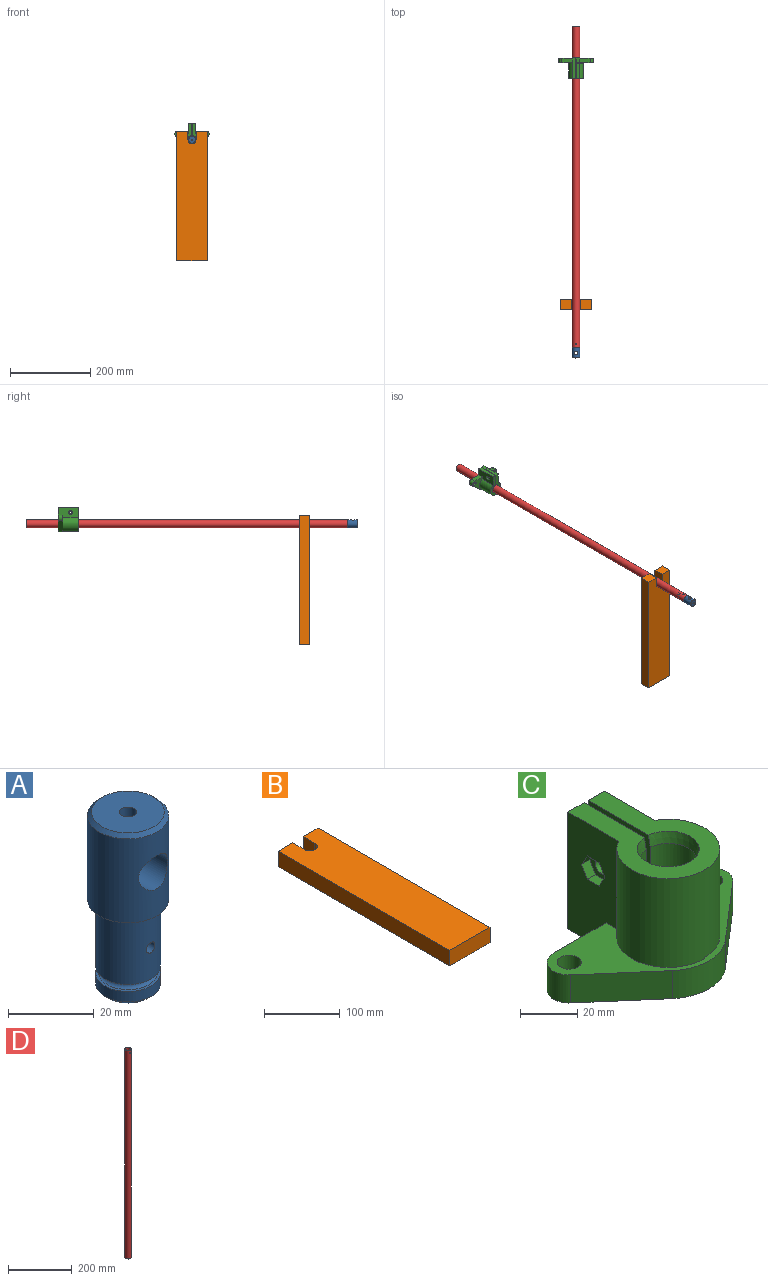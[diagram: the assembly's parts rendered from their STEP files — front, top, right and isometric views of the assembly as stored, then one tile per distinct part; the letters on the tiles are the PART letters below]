
ASSEMBLY  parts=4 mates=3
PART A: 16 faces, bbox 19x19x50 mm
  f0: cylinder r=2mm len=8.19mm, axis (0,0,-1), area 100.1mm2, adj f6,f13
  f1: cylinder r=7.6mm len=15.2mm, axis (0,0,-1), area 143.3mm2, adj f10,f12
  f2: cylinder r=2mm len=33.19mm, axis (0,0,-1), area 399.9mm2, adj f4,f13,f14,f15
  f3: cylinder r=7.6mm len=19.01mm, axis (0,0,-1), area 894.3mm2, adj f7,f9,f14,f15
  f4: plane 13.2x13.2mm, normal (0,0,-1), area 124.3mm2, adj f2,f12
  f5: cylinder r=9.5mm len=24mm, axis (0,0,-1), area 1285.8mm2, adj f7,f11,f13
  f6: plane 17x17mm, normal (0,0,1), area 214.4mm2, adj f0,f11
  f7: plane 19x19mm, normal (0,0,-1), area 102.1mm2, adj f3,f5
  f8: torus R=6.94mm, axis (0,0,1), area 124.5mm2, adj f9,f10
  f9: plane 15.2x15.2mm, normal (0,0,-1), area 26.2mm2, adj f3,f8
  f10: plane 15.2x15.2mm, normal (0,0,1), area 34mm2, adj f1,f8
  f11: cone r=8.5mm half-angle=45deg, axis (0,0,-1), area 80mm2, adj f5,f6
  f12: cone r=7.6mm half-angle=45deg, axis (0,0,1), area 63.1mm2, adj f1,f4
  f13: cylinder r=4.75mm len=19mm, axis (0,-1,0), area 504mm2, adj f0,f2,f5
  f14: cylinder r=1.45mm len=6.22mm, axis (0,-1,0), area 53.1mm2, adj f2,f3
  f15: cylinder r=1.45mm len=6.22mm, axis (0,-1,0), area 53.1mm2, adj f2,f3
PART B: 10 faces, bbox 75x321.6x25 mm
  f0: plane 27.5x25mm, normal (0,1,0), area 687.5mm2, adj f1,f7,f8,f9
  f1: plane 321.58x25mm, normal (-1,0,0), area 8039.4mm2, adj f0,f2,f8,f9
  f2: plane 75x25mm, normal (0,-1,0), area 1875mm2, adj f1,f3,f8,f9
  f3: plane 321.58x25mm, normal (1,0,0), area 8039.4mm2, adj f2,f4,f8,f9
  f4: plane 27.5x25mm, normal (0,1,0), area 687.5mm2, adj f3,f5,f8,f9
  f5: plane 25x21.58mm, normal (-1,0,0), area 539.4mm2, adj f4,f6,f8,f9
  f6: cylinder r=10mm len=25mm, axis (0,0,-1), area 785.4mm2, adj f5,f7,f8,f9
  f7: plane 25x21.58mm, normal (1,0,0), area 539.4mm2, adj f0,f6,f8,f9
  f8: plane 321.58x75mm, normal (0,0,1), area 23529.6mm2, adj f0,f1,f2,f3,f4,f5,f6,f7
  f9: plane 321.58x75mm, normal (0,0,-1), area 23529.6mm2, adj f0,f1,f2,f3,f4,f5,f6,f7
PART C: 40 faces, bbox 85.5x60.7x50 mm
  f0: cylinder r=10mm len=45.28mm, axis (0,0,-1), area 2763.4mm2, adj f1,f2,f16,f17,f28,f29,f39
  f1: plane 37.5x30.72mm, normal (-1,0,0), area 1119.2mm2, adj f0,f25,f27,f28,f38,f39
  f2: plane 50x30.72mm, normal (1,0,0), area 1361.6mm2, adj f0,f7,f16,f17,f26,f27,f37,f39
  f3: plane 12x8mm, normal (0,1,0), area 96mm2, adj f4,f5,f16,f17
  f4: plane 18.92x12mm, normal (1,0,0), area 227mm2, adj f3,f6,f16,f17
  f5: plane 18.92x12mm, normal (-1,0,0), area 227mm2, adj f3,f7,f16,f17
  f6: plane 26x12mm, normal (0,1,0), area 312mm2, adj f4,f13,f16,f17
  f7: plane 12x2mm, normal (0,1,0), area 24mm2, adj f2,f5,f16,f17
  f8: plane 26x12mm, normal (0,1,0), area 312mm2, adj f14,f16,f17,f22
  f9: cylinder r=2.75mm len=5.5mm, axis (0,0,-1), area 51.8mm2, adj f17,f21
  f10: cylinder r=2.75mm len=5.5mm, axis (0,0,-1), area 51.8mm2, adj f17,f19
  f11: cylinder r=20mm len=26.12mm, axis (0,0,-1), area 341.5mm2, adj f12,f15,f16,f17
  f12: plane 27x23.28mm, normal (0.65,-0.76,0), area 427.8mm2, adj f11,f13,f16,f17
  f13: cylinder r=7.75mm len=13.62mm, axis (0,0,-1), area 226mm2, adj f6,f12,f16,f17
  f14: cylinder r=7.75mm len=13.62mm, axis (0,0,-1), area 226mm2, adj f8,f15,f16,f17
  f15: plane 27x23.28mm, normal (-0.65,-0.76,0), area 427.8mm2, adj f11,f14,f16,f17
  f16: plane 85.5x60.67mm, normal (0,0,1), area 1795.2mm2, adj f0,f2,f3,f4,f5,f6,f7,f8
  f17: plane 85.5x60.67mm, normal (0,0,-1), area 2393.3mm2, adj f0,f2,f3,f4,f5,f6,f7,f8
  f18: cylinder r=4.25mm len=9mm, axis (0,0,1), area 240.3mm2, adj f16,f19
  f19: plane 8.5x8.5mm, normal (0,0,1), area 33mm2, adj f10,f18
  f20: cylinder r=4.25mm len=9mm, axis (0,0,1), area 240.3mm2, adj f16,f21
  f21: plane 8.5x8.5mm, normal (0,0,1), area 33mm2, adj f9,f20
  f22: plane 50x25.08mm, normal (-1,0,0), area 1093.4mm2, adj f8,f16,f17,f23,f26,f27,f30,f31
  f23: cylinder r=18mm len=38mm, axis (0,0,-1), area 3557.9mm2, adj f16,f22,f24,f27,f28,f29
  f24: plane 37.5x25.08mm, normal (1,0,0), area 909.7mm2, adj f23,f25,f27,f28,f38
  f25: plane 37.5x8mm, normal (0,1,0), area 300mm2, adj f1,f24,f27,f28
  f26: plane 50x8mm, normal (0,1,0), area 400mm2, adj f2,f17,f22,f27
  f27: plane 58.67x36mm, normal (0,0,1), area 1011.7mm2, adj f1,f2,f22,f23,f24,f25,f26,f39
  f28: plane 58.67x18mm, normal (0,0,-1), area 532.2mm2, adj f0,f1,f23,f24,f25,f29
  f29: plane 8x0.5mm, normal (1,0,0), area 4mm2, adj f0,f16,f23,f28
  f30: plane 5x4mm, normal (0,0.87,0.5), area 23.1mm2, adj f22,f31,f35,f36
  f31: plane 5x4mm, normal (0,0.87,-0.5), area 23.1mm2, adj f22,f30,f32,f36
  f32: plane 5.77x4mm, normal (0,0,-1), area 23.1mm2, adj f22,f31,f33,f36
  f33: plane 5x4mm, normal (0,-0.87,-0.5), area 23.1mm2, adj f22,f32,f34,f36
  f34: plane 5x4mm, normal (0,-0.87,0.5), area 23.1mm2, adj f22,f33,f35,f36
  f35: plane 5.77x4mm, normal (0,0,1), area 23.1mm2, adj f22,f30,f34,f36
  f36: plane 11.55x10mm, normal (-1,0,0), area 55.9mm2, adj f30,f31,f32,f33,f34,f35,f37
  f37: cylinder r=3.12mm len=6.25mm, axis (-1,0,0), area 78.5mm2, adj f2,f36
  f38: cylinder r=3.12mm len=8mm, axis (-1,0,0), area 157.1mm2, adj f1,f24
  f39: cone r=10.83mm half-angle=10deg, axis (0,0,1), area 303.8mm2, adj f0,f1,f2,f27
PART D: 6 faces, bbox 19x19x800 mm
  f0: cylinder r=7.5mm len=800mm, axis (0,0,-1), area 37684.8mm2, adj f2,f3,f4,f5
  f1: cylinder r=9.5mm len=800mm, axis (0,0,-1), area 47738mm2, adj f2,f3,f4,f5
  f2: plane 19x19mm, normal (0,0,1), area 106.8mm2, adj f0,f1
  f3: plane 19x19mm, normal (0,0,-1), area 106.8mm2, adj f0,f1
  f4: cylinder r=1.5mm len=3mm, axis (0,-1,0), area 19mm2, adj f0,f1
  f5: cylinder r=1.5mm len=3mm, axis (0,-1,0), area 19mm2, adj f0,f1
PLACE A rot(axis=(1,0,0),90deg) t=(-75.37,-695.45,0)mm
PLACE B rot(axis=(1,0,0),90deg) t=(0,-100,0)mm
PLACE C rot(axis=(1,0,0),90deg) t=(0,0,0)mm
PLACE D rot(axis=(1,0,0),90deg) t=(0,179.55,0)mm
MATE slider C.f0 <-> D.f0  axis (0,1,0) through (0,0,0)mm
MATE fastened D.f0 <-> A.f0  axis (0,-1,0) through (0,-720.45,0)mm
MATE fastened C.f0 <-> B.f6  axis (0,1,0) through (0,0,0)mm
